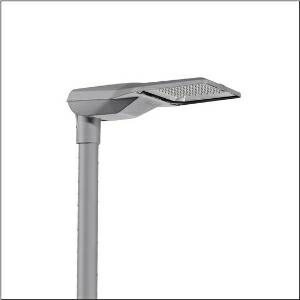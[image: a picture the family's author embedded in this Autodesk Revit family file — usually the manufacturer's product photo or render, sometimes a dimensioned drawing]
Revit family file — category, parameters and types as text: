
# Revit family: streetlight_sl_21_iq_midi___st0_8a_5xe3c41g08nb_9f8f
name_source: partatom
category: Lighting Fixtures
units: mm (PartAtom-declared; Revit-internal decimal feet)

## family parameters
Cut with Voids When Loaded = No
Host = Face
Light Source = No
Part Type = Normal
Room Calculation Point = No
Round Connector Dimension = Use Diameter
Shared = No

## types (1)
- --- (1 x LED, 24250 lm, 155.5 W, 4000K)
    Apparent Load = 155 VA
    CIE Flux Codes = 41 75 97 100 100
    Color Rendering = 70
    Color Temperature = 4000K
    Default Elevation = 1800 mm
    Description = Streetlight SL 21 iQ midi, mast luminaire, primary light control with lens, of PMMA, primary optical cover: cover, of toughened safety glass, transparent, light distribution: ST0.8a, light emission: direct distribution, primary light characteristic: asymmetric, installation type: post-top, side-entry, LED, High Power LED, rated luminous flux: 24.250lm, luminous efficacy: 156lm/W, light colour: 740, colour temperature: 4000K, control gear: iQ Street-Remote, control: Street-Remote, Auto-Match, Temp-Guard, Lumen-Switch, Night-Set, Smart-Wire, Light-Fading, Desk-Remote (wireless, voltage-free reading and setting of iQ features in the workshop via application-optimized NFC function/RFID function), optimised constant luminous flux control (CLO 2.0), pre-setting: linear dimming characteristic, mains connection: 230..240V, AC, 50/60Hz, start of lifetime: 156W, end of service life: 162W, reduction: 69W, luminaire housing, of diecast aluminium, powder-coated, Siteco® metallic grey (DB 702S), corrosivity category C5 mid according to DIN EN ISO 12944, please order mast flange separately, inclination adjustable: 0°, 5°, 10°, 15°, sealing non-destructively replaceable, multi-level sealing system, length: 644mm, width: 335mm, height: 110mm, mast flange for spigot size: 42mm (side-entry): 5XC10008XM4, 60/48mm (side-entry/post-top): 5XC10108XM2, 76/60mm (side-entry/post-top): 5XC10108XM1, mounting height: 4..8m, protection rating (complete): IP66, insulation class (complete): insulation class II (safety insulation), certification: CE, ENEC, ENEC+, VDE, impact resistance: IK10, permissible operating ambient temperature for outdoor applications: -40..+50°C, standard-compliant lighting for roads and squares, packaging unit: 1 piece

Light Distribution: ST0.8a
    Height = 111 mm
    Lamp = 1 x LED
    Lamp Light Flux = 24250 lm
    Lamp Power = 155.5 W
    Lamp count = 1
    Length = 644 mm
    Luminous efficacy = 156 lm/W
    Manufacturer = Siteco
    ModVariant = No
    Model = 5XE3C41G08NB
    Number of Poles = 1
    OnlyDefault = Yes
    Power Factor = 1
    Product Name = Streetlight SL 21 iQ midi | ST0.8a
    Product group = mast luminaire | pylon top
    ProductGroupID = 6100
    Protection Class = Protection class II
    Protection Degree = IP 66
    RLX_Detail_Level = 1
    RLX_Emergency_Light_Flux = 0 lm
    RLX_Emergency_Type = 0
    RLX_Emergency_Type_DB = No
    RlxData = <blob elided: 27169 chars, md5=38d9cc03>
    Socket = socket
    Standby Power = 0 W
    System Light Flux = 24250 lm
    System Power = 155 W
    Type Comments = factory setting: luminous flux: 100 % | dim-lin: 254 | 823 mA
    Type Image = l_1004298.jpg
    URL = http://relux.com
    VarID = @adj_190341
    Voltage = 0 V
    Weight = 0.00 kg
    Width = 336 mm

## geometry (parser evidence)
native form markers: Blend x4, Sweep x13
no freeform markers — native parametric forms only
